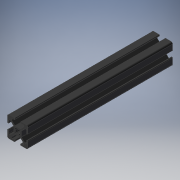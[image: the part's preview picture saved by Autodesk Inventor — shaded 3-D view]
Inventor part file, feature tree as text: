
AUTODESK INVENTOR PART (.ipt)
format: ipt  version: 2019 (Build 230136000, 136)  size: 237,568 bytes
history: native  units: mm
features: extrude x1, sketch x1
ambient origin geometry x8: Origin, YZ Plane, XZ Plane, XY Plane, X Axis, Y Axis, Z Axis, Center Point
bodies: Solid1 (feature_tree)
feature tree (2):
  extrude  "Extrusion1"  [1 undecoded]
  sketch  "Sketch_1"  dims[d0=140.25mm d1=0.0mm]
note: 1 required parameter value undecoded (feature->parameter linkage not recoverable at this tier; creation-order binding heuristic only, values carry confidence <= 0.55)
